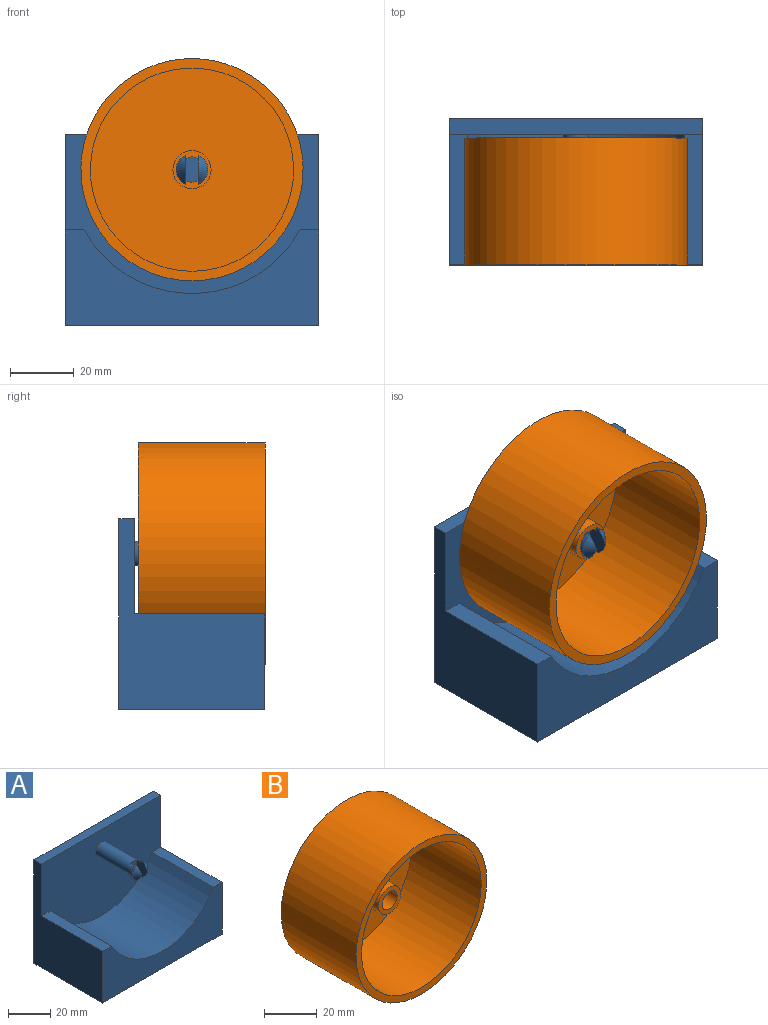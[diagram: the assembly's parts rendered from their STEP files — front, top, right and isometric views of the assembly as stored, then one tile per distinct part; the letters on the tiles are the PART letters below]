
ASSEMBLY  parts=2 mates=1
PART A: 20 faces, bbox 80x46x60 mm
  f0: cylinder r=5mm len=9.17mm, axis (0,-1,0), area 11.6mm2, adj f3,f16,f19
  f1: cylinder r=5mm len=9.17mm, axis (0,-1,0), area 11.6mm2, adj f14,f17,f18
  f2: cylinder r=4mm len=25mm, axis (0,1,0), area 603.2mm2, adj f3,f11,f14,f15,f16,f17
  f3: plane 9.17x3mm, normal (0,1,0), area 10mm2, adj f0,f2,f16
  f4: plane 60x46mm, normal (1,0,0), area 1530mm2, adj f5,f6,f9,f10,f11,f12
  f5: plane 80x5mm, normal (0,0,1), area 400mm2, adj f4,f8,f10,f11
  f6: plane 80x30mm, normal (0,-1,0), area 1431.9mm2, adj f4,f7,f8,f9,f12,f13
  f7: cylinder r=39mm len=68.12mm, axis (0,-1,0), area 3396.1mm2, adj f6,f11,f12,f13
  f8: plane 60x46mm, normal (-1,0,0), area 1530mm2, adj f5,f6,f9,f10,f11,f13
  f9: plane 80x46mm, normal (0,0,-1), area 3680mm2, adj f4,f6,f8,f10
  f10: plane 80x60mm, normal (0,1,0), area 4800mm2, adj f4,f5,f8,f9
  f11: plane 80x50mm, normal (0,-1,0), area 3317.8mm2, adj f2,f4,f5,f7,f8,f12,f13
  f12: plane 41x5.94mm, normal (0,0,1), area 243.6mm2, adj f4,f6,f7,f11
  f13: plane 41x5.94mm, normal (0,0,1), area 243.6mm2, adj f6,f7,f8,f11
  f14: plane 9.17x3mm, normal (0,1,0), area 10mm2, adj f1,f2,f17
  f15: plane 8x4mm, normal (0,-1,0), area 30.6mm2, adj f2,f16,f17
  f16: plane 9.17x7mm, normal (-1,0,0), area 46.6mm2, adj f0,f2,f3,f15,f19
  f17: plane 9.17x7mm, normal (1,0,0), area 46.6mm2, adj f1,f2,f14,f15,f18
  f18: cone r=1mm half-angle=45deg, axis (0,1,0), area 28mm2, adj f1,f17
  f19: cone r=1mm half-angle=45deg, axis (0,1,0), area 28mm2, adj f0,f16
PART B: 8 faces, bbox 70x40x70 mm
  f0: cylinder r=35mm len=70mm, axis (0,1,0), area 8796.5mm2, adj f1,f2
  f1: plane 70x70mm, normal (0,-1,0), area 631.5mm2, adj f0,f3
  f2: plane 70x70mm, normal (0,1,0), area 3798.2mm2, adj f0,f7
  f3: cylinder r=32mm len=64mm, axis (0,-1,0), area 7439.3mm2, adj f1,f4
  f4: plane 64x64mm, normal (0,-1,0), area 3103.9mm2, adj f3,f5
  f5: cylinder r=6mm len=20mm, axis (0,1,0), area 754mm2, adj f4,f6
  f6: plane 12x12mm, normal (0,-1,0), area 62.8mm2, adj f5,f7
  f7: cylinder r=4mm len=23mm, axis (0,-1,0), area 578.1mm2, adj f2,f6
PLACE A t=(-7.68,4.81,-22.7)mm
PLACE B t=(-7.68,-1.27,-3.7)mm
MATE slider B.f5 <-> A.f7  axis (0,1,0) through (-7.68,-24.27,-3.7)mm
